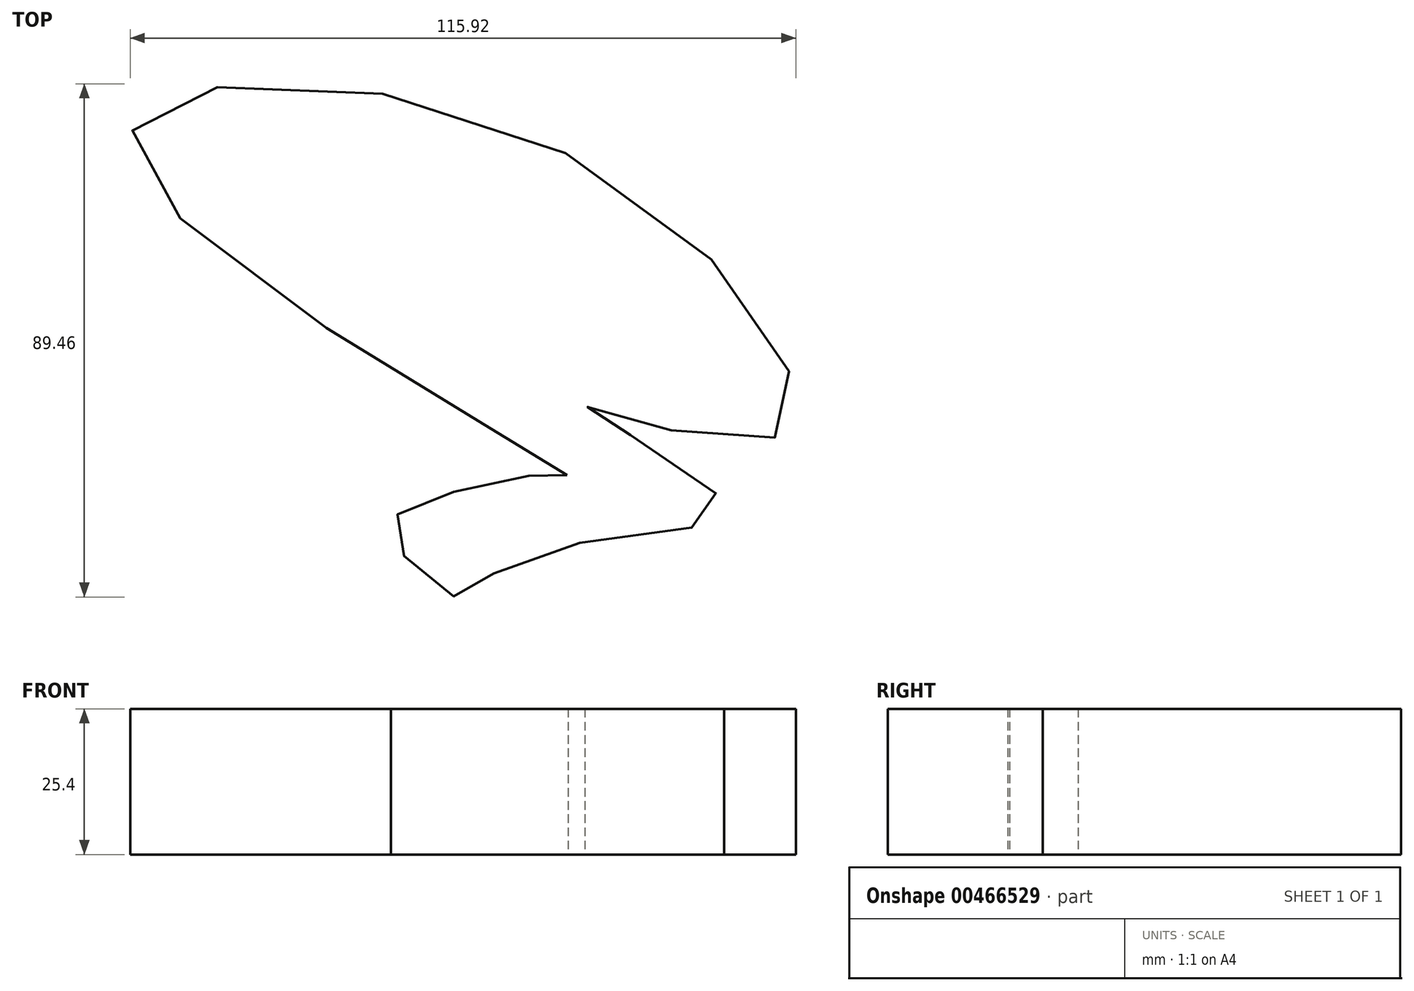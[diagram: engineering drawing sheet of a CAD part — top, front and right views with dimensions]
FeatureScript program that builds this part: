
annotation { "Feature Type Name" : "Feature", "Feature Type Description" : "" }
export const myFeature = defineFeature(function(context is Context, id is Id, definition is map)
    precondition{}
    {
        {
            var Q0;
            Q0=qCreatedBy(makeId("Top.planeOp"),FACE);
            var sketch = newSketch(context, id + "F0", { "sketchPlane" : qUnion([Q0])});
            skFitSpline(sketch, "E0", {"points": [v(0, 0) * mm, v(-75.86, 56.18) * mm, v(0, 55.96) * mm, v(36.29, 6.56) * mm, v(3.06, 11.8) * mm, v(27.33, -5.47) * mm, v(-7.87, -14.2) * mm, v(-19.46, -21.2) * mm, v(-30.6, -9.84) * mm, v(-26.01, -5.03) * mm, v(-3.5, 0) * mm, v(0, 0) * mm]});
            skSolve(sketch);
        }
        {
            var Q0;
            Q0 = qSketchRegion(id + "F0", true);
            extrude(context, id + "F1", {"entities" : qUnion([Q0]), "depth" : 25.4 * mm});
        }
    });
